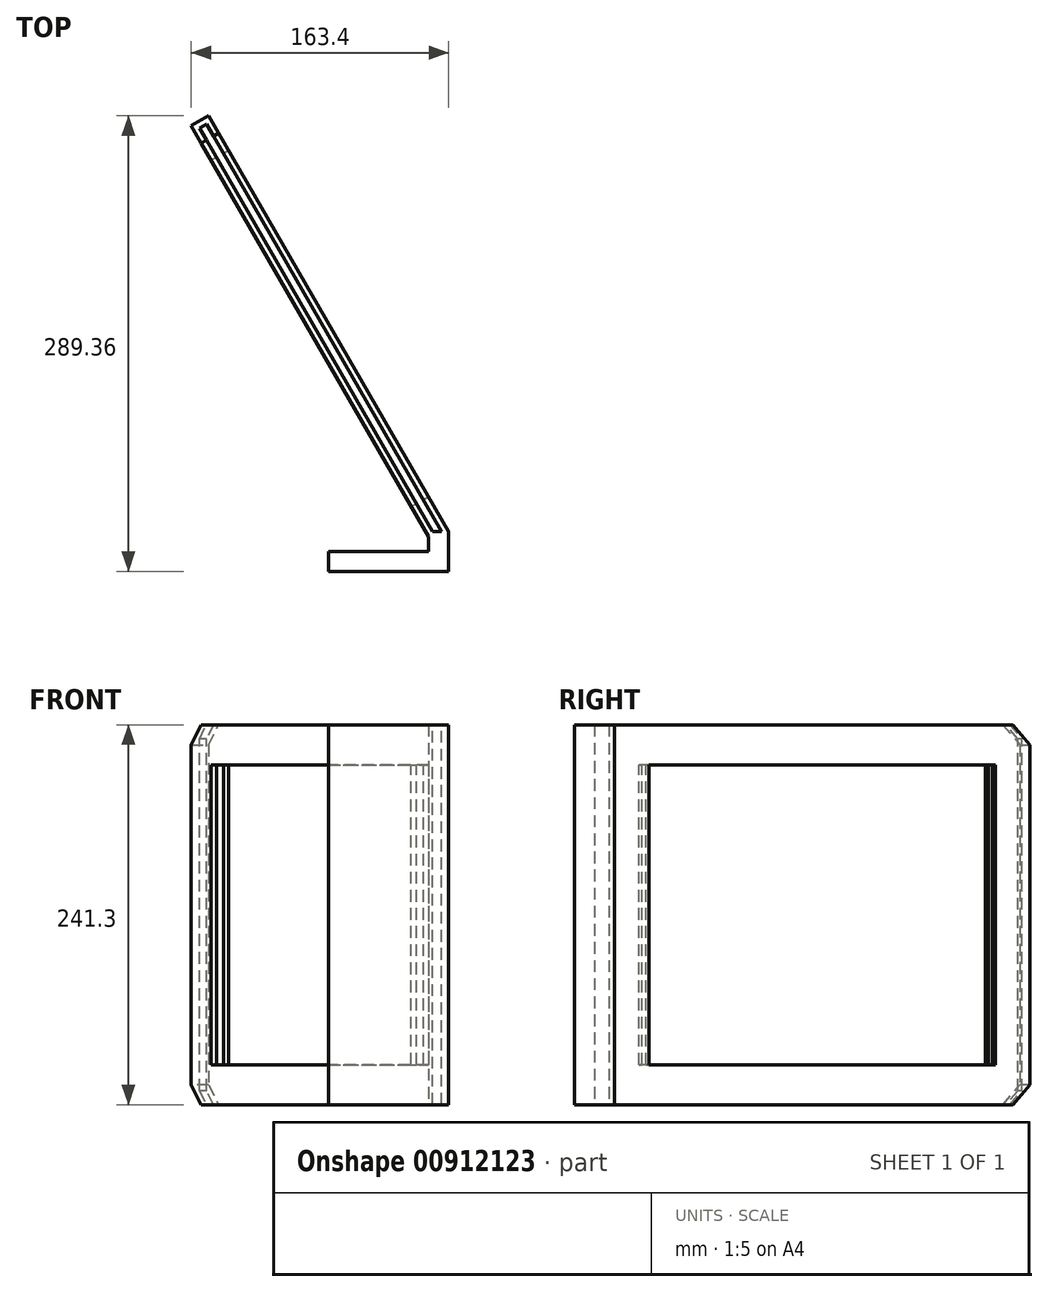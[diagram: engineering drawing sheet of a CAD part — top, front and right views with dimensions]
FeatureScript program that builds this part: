
annotation { "Feature Type Name" : "Feature", "Feature Type Description" : "" }
export const myFeature = defineFeature(function(context is Context, id is Id, definition is map)
    precondition{}
    {
        {
            var Q0;
            Q0=qCreatedBy(makeId("Top.planeOp"),FACE);
            var sketch = newSketch(context, id + "F0", { "sketchPlane" : qUnion([Q0])});
            skLineSegment(sketch, "E0", {"start": v(0, 0) * mm, "end": v(76.2, 0) * mm});
            skLineSegment(sketch, "E1", {"start": v(76.2, 0) * mm, "end": v(76.2, 25.4) * mm});
            skLineSegment(sketch, "E2", {"start": v(76.2, 25.4) * mm, "end": v(-76.2, 289.36) * mm});
            skLineSegment(sketch, "E3.0", {"start": v(63.5, 22) * mm, "end": v(-87.2, 283.01) * mm});
            skLineSegment(sketch, "E3.1", {"start": v(63.5, 12.7) * mm, "end": v(63.5, 22) * mm});
            skLineSegment(sketch, "E3.2", {"start": v(0, 12.7) * mm, "end": v(63.5, 12.7) * mm});
            skLineSegment(sketch, "E4", {"start": v(0, 12.7) * mm, "end": v(0, 0) * mm});
            skLineSegment(sketch, "E5", {"start": v(-76.2, 289.36) * mm, "end": v(-87.2, 283.01) * mm});
            skSolve(sketch);
        }
        {
            var Q0;
            Q0=makeQuery(id+"F0.imprint","IMPRINT",FACE,{"disambiguationData":[TD([[makeQuery(id+"F0.imprint","IMPRINT",EDGE,{"derivedFrom":sQuery(id+"F0.wireOp",EDGE,"E0")}),1.0]])]});
            extrude(context, id + "F1", {"entities" : qUnion([Q0]), "depth" : 241.3 * mm, "offsetDistance" : 25.4 * mm});
        }
        {
            var Q0;
            Q0=makeQuery(id+"F1.opExtrude","SWEPT_FACE",FACE,{"disambiguationData":[OSD([sQuery(id+"F0.wireOp",EDGE,"E2")])]});
            var sketch = newSketch(context, id + "F2", { "sketchPlane" : qUnion([Q0])});
            skLineSegment(sketch, "E6.0", {"start": v(263.3, 215.9) * mm, "end": v(263.3, 25.4) * mm});
            skLineSegment(sketch, "E6.1", {"start": v(9.3, 215.9) * mm, "end": v(263.3, 215.9) * mm});
            skLineSegment(sketch, "E6.2", {"start": v(9.3, 215.9) * mm, "end": v(9.3, 25.4) * mm});
            skLineSegment(sketch, "E6.3", {"start": v(9.3, 25.4) * mm, "end": v(263.3, 25.4) * mm});
            skSolve(sketch);
        }
        {
            var Q0;
            Q0=makeQuery(id+"F2.imprint","IMPRINT",FACE,{"disambiguationData":[TD([[makeQuery(id+"F2.imprint","IMPRINT",EDGE,{"derivedFrom":sQuery(id+"F2.wireOp",EDGE,"E6.0")}),-1.0]])]});
            extrude(context, id + "F3", {"entities" : qUnion([Q0]), "operationType" : NewBodyOperationType.REMOVE, "oppositeDirection" : true, "depth" : 25.4 * mm, "offsetDistance" : 25.4 * mm});
        }
        {
            var Q0;
            Q0=makeQuery(id+"F1.opExtrude","CAP_FACE",FACE,{"disambiguationData":[OSD([sQuery(id+"F0.wireOp",EDGE,"E0"),sQuery(id+"F0.wireOp",EDGE,"E1"),sQuery(id+"F0.wireOp",EDGE,"E2"),sQuery(id+"F0.wireOp",EDGE,"E3.0"),sQuery(id+"F0.wireOp",EDGE,"E3.1"),sQuery(id+"F0.wireOp",EDGE,"E3.2"),sQuery(id+"F0.wireOp",EDGE,"E4"),sQuery(id+"F0.wireOp",EDGE,"E5")])],"isStart":false});
            var sketch = newSketch(context, id + "F4", { "sketchPlane" : qUnion([Q0])});
            skLineSegment(sketch, "E7.0", {"start": v(65.93, 25.4) * mm, "end": v(-82, 281.62) * mm});
            skLineSegment(sketch, "E7.1", {"start": v(-77.6, 284.16) * mm, "end": v(-82, 281.62) * mm});
            skLineSegment(sketch, "E7.2", {"start": v(71.8, 25.4) * mm, "end": v(-77.6, 284.16) * mm});
            skLineSegment(sketch, "E8", {"start": v(71.8, 25.4) * mm, "end": v(65.93, 25.4) * mm});
            skPoint(sketch, "E9.orphan", {"position": v(88.37, 25.4) * mm});
            skSolve(sketch);
        }
        {
            var Q0;
            Q0=makeQuery(id+"F4.imprint","IMPRINT",FACE,{"disambiguationData":[TD([[makeQuery(id+"F4.imprint","IMPRINT",EDGE,{"derivedFrom":sQuery(id+"F4.wireOp",EDGE,"E7.0")}),-1.0]])]});
            extrude(context, id + "F5", {"entities" : qUnion([Q0]), "operationType" : NewBodyOperationType.REMOVE, "oppositeDirection" : true, "depth" : 508 * mm, "offsetDistance" : 25.4 * mm});
        }
        {
            var Q0;
            Q0=makeQuery(id+"F1.opExtrude","CAP_EDGE",EDGE,{"disambiguationData":[OSD([sQuery(id+"F0.wireOp",EDGE,"E5")])],"isStart":true});
            chamfer(context, id + "F6", {"entities" : qUnion([Q0]), "width" : 12.7 * mm, "tangentPropagation" : true});
        }
        {
            var Q0;
            Q0=makeQuery(id+"F1.opExtrude","CAP_EDGE",EDGE,{"disambiguationData":[OSD([sQuery(id+"F0.wireOp",EDGE,"E5")])],"isStart":false});
            chamfer(context, id + "F7", {"entities" : qUnion([Q0]), "width" : 12.7 * mm, "tangentPropagation" : true});
        }
    });
